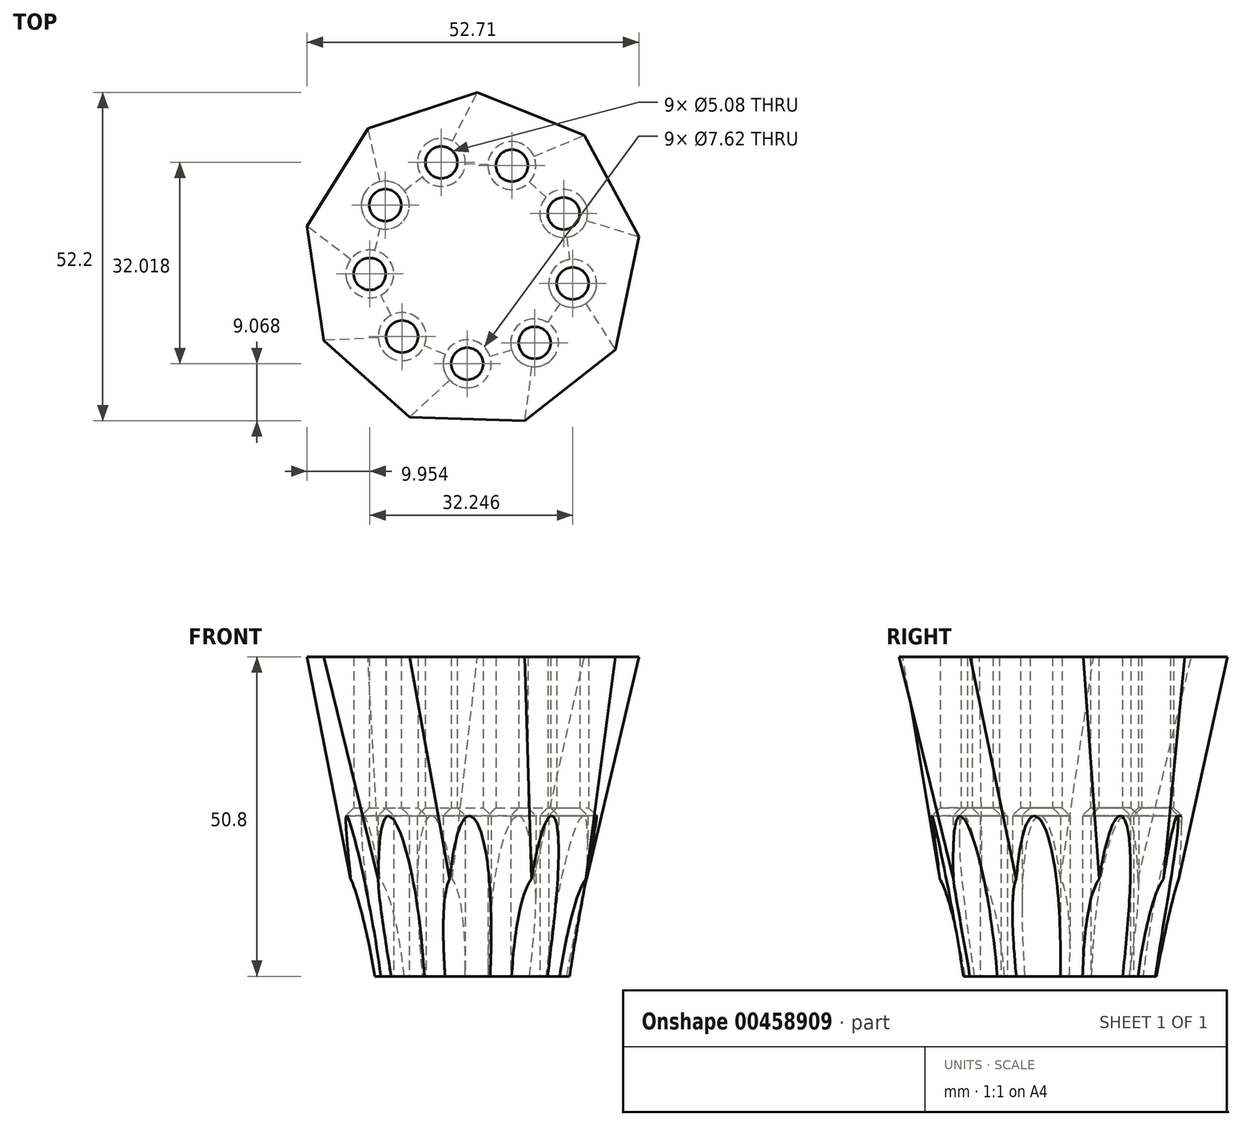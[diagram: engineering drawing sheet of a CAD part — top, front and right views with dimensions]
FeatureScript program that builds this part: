
annotation { "Feature Type Name" : "Feature", "Feature Type Description" : "" }
export const myFeature = defineFeature(function(context is Context, id is Id, definition is map)
    precondition{}
    {
        {
            var Q0;
            Q0=qCreatedBy(makeId("Top.planeOp"),FACE);
            cPlane(context, id + "F0", {"entities" : qUnion([Q0]), "cplaneType" : CPlaneType.OFFSET, "offset" : 50.8 * mm, "width" : 152.4 * mm, "height" : 152.4 * mm});
        }
        {
            var Q0;
            Q0=qCreatedBy(makeId("Top.planeOp"),FACE);
            var sketch = newSketch(context, id + "F1", { "sketchPlane" : qUnion([Q0])});
            skCircle(sketch, "E0.cCircle", {"center": v(0, 0) * mm, "radius": 15.4 * mm, "construction": true});
            skLineSegment(sketch, "E0.0", {"start": v(16, -3.6) * mm, "end": v(9.94, -13.03) * mm});
            skLineSegment(sketch, "E0.1", {"start": v(9.94, -13.03) * mm, "end": v(-0.76, -16.37) * mm});
            skLineSegment(sketch, "E0.2", {"start": v(-0.76, -16.37) * mm, "end": v(-11.1, -12.05) * mm});
            skLineSegment(sketch, "E0.3", {"start": v(-11.1, -12.05) * mm, "end": v(-16.26, -2.09) * mm});
            skLineSegment(sketch, "E0.4", {"start": v(-16.26, -2.09) * mm, "end": v(-13.8, 8.85) * mm});
            skLineSegment(sketch, "E0.5", {"start": v(-13.8, 8.85) * mm, "end": v(-4.88, 15.65) * mm});
            skLineSegment(sketch, "E0.6", {"start": v(-4.88, 15.65) * mm, "end": v(6.32, 15.12) * mm});
            skLineSegment(sketch, "E0.7", {"start": v(6.32, 15.12) * mm, "end": v(14.56, 7.52) * mm});
            skLineSegment(sketch, "E0.8", {"start": v(14.56, 7.52) * mm, "end": v(16, -3.6) * mm});
            skPoint(sketch, "E0.0.midPoint", {"position": v(12.96, -8.31) * mm});
            skSolve(sketch);
        }
        {
            var Q0;
            Q0=qCreatedBy(id+"F0.planeOp",FACE);
            var sketch = newSketch(context, id + "F2", { "sketchPlane" : qUnion([Q0])});
            skCircle(sketch, "E1.cCircle", {"center": v(0, 0) * mm, "radius": 25.16 * mm, "construction": true});
            skLineSegment(sketch, "E1.0", {"start": v(17.85, 19.96) * mm, "end": v(26.5, 3.82) * mm});
            skLineSegment(sketch, "E1.1", {"start": v(26.5, 3.82) * mm, "end": v(22.75, -14.11) * mm});
            skLineSegment(sketch, "E1.2", {"start": v(22.75, -14.11) * mm, "end": v(8.36, -25.44) * mm});
            skLineSegment(sketch, "E1.3", {"start": v(8.36, -25.44) * mm, "end": v(-9.95, -24.86) * mm});
            skLineSegment(sketch, "E1.4", {"start": v(-9.95, -24.86) * mm, "end": v(-23.6, -12.65) * mm});
            skLineSegment(sketch, "E1.5", {"start": v(-23.6, -12.65) * mm, "end": v(-26.2, 5.48) * mm});
            skLineSegment(sketch, "E1.6", {"start": v(-26.2, 5.48) * mm, "end": v(-16.56, 21.04) * mm});
            skLineSegment(sketch, "E1.7", {"start": v(-16.56, 21.04) * mm, "end": v(0.84, 26.76) * mm});
            skLineSegment(sketch, "E1.8", {"start": v(0.84, 26.76) * mm, "end": v(17.85, 19.96) * mm});
            skPoint(sketch, "E1.0.midPoint", {"position": v(22.17, 11.89) * mm});
            skSolve(sketch);
        }
        {
            var Q0;
            Q0=makeQuery(id+"F1.imprint","IMPRINT",FACE,{"disambiguationData":[TD([[makeQuery(id+"F1.imprint","IMPRINT",EDGE,{"derivedFrom":sQuery(id+"F1.wireOp",EDGE,"E0.0")}),-1.0]])]});
            var Q1;
            Q1=makeQuery(id+"F2.imprint","IMPRINT",FACE,{"disambiguationData":[TD([[makeQuery(id+"F2.imprint","IMPRINT",EDGE,{"derivedFrom":sQuery(id+"F2.wireOp",EDGE,"E1.0")}),-1.0]])]});
            loft(context, id + "F3", {"sheetProfilesArray" : [{ "sheetProfileEntities" : qUnion([Q0]) }, { "sheetProfileEntities" : qUnion([Q1]) }]});
        }
        {
            var Q0;
            Q0=sQuery(id+"F1.wireOp",VERTEX,"E0.1.start");
            var Q1;
            Q1=sQuery(id+"F1.wireOp",VERTEX,"E0.7.end");
            var Q2;
            Q2=sQuery(id+"F1.wireOp",VERTEX,"E0.6.start");
            var Q3;
            Q3=sQuery(id+"F1.wireOp",VERTEX,"E0.0.start");
            var Q4;
            Q4=sQuery(id+"F1.wireOp",VERTEX,"E0.2.start");
            var Q5;
            Q5=sQuery(id+"F1.wireOp",VERTEX,"E0.3.start");
            var Q6;
            Q6=sQuery(id+"F1.wireOp",VERTEX,"E0.4.start");
            var Q7;
            Q7=sQuery(id+"F1.wireOp",VERTEX,"E0.5.start");
            var Q8;
            Q8=sQuery(id+"F1.wireOp",VERTEX,"E0.7.start");
            var Q9;
            Q9=makeQuery(id+"F3.opLoft","SWEPT_BODY",BODY,{"disambiguationData":[OSD([makeQuery(id+"F1.imprint","IMPRINT",FACE,{"disambiguationData":[TD([[makeQuery(id+"F1.imprint","IMPRINT",EDGE,{"derivedFrom":sQuery(id+"F1.wireOp",EDGE,"E0.0")}),-1.0]])]}),makeQuery(id+"F2.imprint","IMPRINT",FACE,{"disambiguationData":[TD([[makeQuery(id+"F2.imprint","IMPRINT",EDGE,{"derivedFrom":sQuery(id+"F2.wireOp",EDGE,"E1.0")}),-1.0]])]})])]});
            hole(context, id + "F4", {"style" : HoleStyle.C_SINK, "endStyle" : HoleEndStyle.THROUGH, "oppositeDirection" : true, "holeDiameter" : 5.08 * mm, "cSinkDiameter" : 7.62 * mm, "cSinkAngle" : 90 * degree, "isTappedThrough" : true, "tappedDepth" : 12.7 * mm, "tapClearance" : 3, "locations" : qUnion([Q0, Q1, Q2, Q3, Q4, Q5, Q6, Q7, Q8]), "scope" : qUnion([Q9])});
        }
    });
